# Revit family: ROSENBERG_KBAE_180-400
name_source: partatom
category: Wyposażenie mechaniczne
revit_build: Autodesk Revit MEP 2016 (Build: 20150220_1215(x64)
units: mm (PartAtom-declared; Revit-internal decimal feet)

## family parameters
Numer OmniClass = 23.75.00.00
Oparty na płaszczyźnie roboczej = Tak
Punkt obliczania pomieszczeń = Nie
Tnij formami wycięć po wczytaniu = Nie
Typ części = Normalny
Tytuł OmniClass = Climate Control (HVAC)
Współdzielony = Nie
Wymiar okrągłego złącza = Użyj średnicy
Zawsze pionowo = Tak

## types (8) — shared parameters
1.param.H.podstawa = 29 mm  [stored 0.0951444 ft]
1.param.W.podstawa = 38 mm  [stored 0.124672 ft]
1.param.odsunięcie.urządzenie.front = 35 mm  [stored 0.114829 ft]
2.param.szer.klapa = 60 mm  [stored 0.19685 ft]
5.param.h.wylot = 45 mm
Charakterystyka pracy = https://rosenberg.pl
Częstotliwość pracy = 50 Hz
Domyślna rzędna = 1219 mm
Materiał = <Wg kategorii>
Napięcie znamionowe = 230 V
Opis = Wentylator do okapów kuchennych
Producent = Rosenberg
Typ zasilania = 1
URL = https://rosenberg.pl
Wysokość kroćca = 45 mm
param.lb.otwor = 10
param.odl.rączka = 55 mm
param.otwory. = 5 mm  [stored 0.0164042 ft]
param.puszka.przył = 140 mm

## per-type parameters (varying)
| type | 1.param.dł.podstawa | 2.param.H.urządzenia | 2.param.W.urządzenia | 2.param.szer.urządzenie | 3.param.L.tyl.went | 4.param.h.wlot | 4.param.odsunięcie.wlot | 5.param.odsunięcie.wylot | 5.param.os.went.wyw | Klasa szczelności | Masa | Moc znamionowa | Numer katalogowy | Prąd znamionowy | param.L.otwor | param.otw.wew | param.void | Średnica przyłącza |
| KBAE 400-4SW.120 | 800 mm | 665 mm | 770 mm | 331 mm | 492 mm | 372 mm | 451 mm | 207 mm | 163 mm | IP54 | 71.00 kg | 450 W | B21-40017 | 2 A | 143 mm | 300 mm | 345 mm | 355 mm |
| KBAE 355-4SW.110 | 800 mm | 665 mm | 770 mm | 331 mm | 472 mm | 372 mm | 451 mm | 207 mm | 163 mm | IP54 | 70.00 kg | 290 W | B21-35517 | 1 A | 143 mm | 300 mm | 345 mm | 355 mm |
| KBAE 315-4SW.098 | 800 mm | 600 mm | 690 mm | 307 mm | 448 mm | 339 mm | 398 mm | 188 mm | 154 mm | IP54 | 67.00 kg | 200 W | B21-31517 | 1 A | 143 mm | 270 mm | 305 mm | 315 mm |
| KBAE 280-4ST.114 | 600 mm | 537 mm | 625 mm | 291 mm | 480 mm | 295 mm | 360 mm | 172 mm | 143 mm | IP21 | 64.00 kg | 1400 W | B21-28017 | 6 A | 143 mm | 260 mm | 270 mm | 280 mm |
| KBAE 250-4ST.102 | 600 mm | 500 mm | 576 mm | 272 mm | 461 mm | 282 mm | 333 mm | 162 mm | 133 mm | IP54 | 56.00 kg | 1100 W | B21-25017 | 6 A | 51 mm | 240 mm | 240 mm | 250 mm |
| KBAE 225-4ST.092 | 600 mm | 445 mm | 522 mm | 251 mm | 413 mm | 256 mm | 301 mm | 147 mm | 123 mm | IP54 | 37.00 kg | 490 W | B21-22517 | 2 A | 51 mm | 215 mm | 215 mm | 225 mm |
| KBAE 200-4ST.082 | 450 mm | 445 mm | 450 mm | 232 mm | 373 mm | 249 mm | 292 mm | 143 mm | 113 mm | IP54 | 31.50 kg | 310 W | B21-20017 | 1 A | 51 mm | 190 mm | 190 mm | 200 mm  [stored 0.656168 ft] |
| KBAE 180-4ST.082 | 450 mm | 412 mm | 470 mm | 221 mm | 362 mm | 230 mm | 269 mm | 134 mm | 107 mm | IP54 | 31.50 kg | 240 W | B21-18017 | 1 A | 51 mm | 190 mm | 190 mm | 200 mm  [stored 0.656168 ft] |

note: column(s) folded — value = type name in every type: Model

note: [stored X ft] marks values corroborated as IEEE doubles in the binary element streams (Revit-internal decimal feet)

## geometry (parser evidence)
native form markers: Blend x2, Sweep x3
no freeform markers — native parametric forms only
